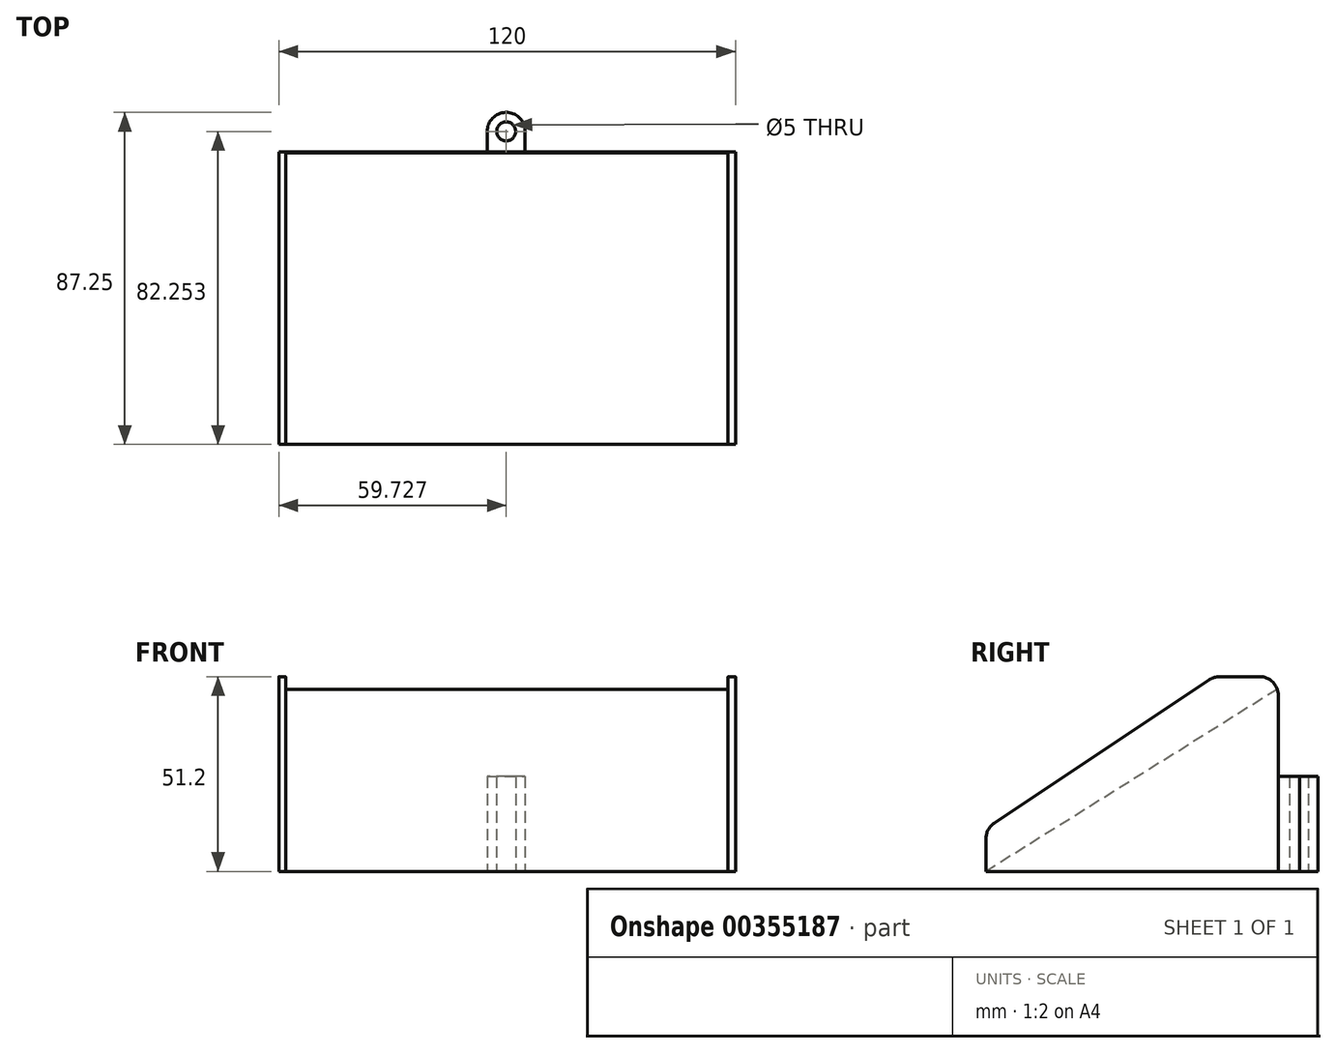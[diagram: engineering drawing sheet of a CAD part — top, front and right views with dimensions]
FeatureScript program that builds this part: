
annotation { "Feature Type Name" : "Feature", "Feature Type Description" : "" }
export const myFeature = defineFeature(function(context is Context, id is Id, definition is map)
    precondition{}
    {
        {
            var Q0;
            Q0=qCreatedBy(makeId("Top.planeOp"),FACE);
            var sketch = newSketch(context, id + "F0", { "sketchPlane" : qUnion([Q0])});
            skLineSegment(sketch, "E0.bottom", {"start": v(-59.62, 37.09) * mm, "end": v(60.38, 37.09) * mm});
            skLineSegment(sketch, "E0.top", {"start": v(-59.62, -39.78) * mm, "end": v(60.38, -39.78) * mm});
            skLineSegment(sketch, "E0.left", {"start": v(-59.62, 37.09) * mm, "end": v(-59.62, -39.78) * mm});
            skLineSegment(sketch, "E0.right", {"start": v(60.38, 37.09) * mm, "end": v(60.38, -39.78) * mm});
            skLineSegment(sketch, "E1", {"start": v(-57.82, 37.09) * mm, "end": v(-57.82, -39.78) * mm});
            skLineSegment(sketch, "E2", {"start": v(58.4, 37.09) * mm, "end": v(58.4, -39.78) * mm});
            skCircle(sketch, "E3", {"center": v(0.1, 42.47) * mm, "radius": 5 * mm});
            skCircle(sketch, "E4", {"center": v(0.1, 42.47) * mm, "radius": 2.5 * mm});
            skLineSegment(sketch, "E5", {"start": v(5.1, 42.69) * mm, "end": v(5.1, 37.09) * mm});
            skLineSegment(sketch, "E6", {"start": v(-4.9, 42.47) * mm, "end": v(-4.9, 37.09) * mm});
            skSolve(sketch);
        }
        {
            var Q0;
            Q0=makeQuery(id+"F0.imprint","IMPRINT",FACE,{"disambiguationData":[TD([[makeQuery(id+"F0.imprint","IMPRINT",EDGE,{"derivedFrom":sQuery(id+"F0.wireOp",EDGE,"E0.bottom")}),-1.0]])]});
            extrude(context, id + "F1", {"entities" : qUnion([Q0]), "depth" : 50 * mm});
        }
        {
            var Q0;
            Q0=makeQuery(id+"F1.opExtrude","CAP_EDGE",EDGE,{"disambiguationData":[OSD([sQuery(id+"F0.wireOp",EDGE,"E0.top")])],"isStart":false});
            chamfer(context, id + "F2", {"entities" : qUnion([Q0]), "chamferType" : ChamferType.TWO_OFFSETS, "width1" : 80 * mm, "oppositeDirection" : false, "width2" : 50 * mm, "tangentPropagation" : true});
        }
        {
            var Q0;
            Q0=makeQuery(id+"F0.imprint","IMPRINT",FACE,{"disambiguationData":[TD([[makeQuery(id+"F0.imprint","IMPRINT",EDGE,{"derivedFrom":sQuery(id+"F0.wireOp",EDGE,"E3")}),1.0]])]});
            var Q1;
            {var subQ3=sQuery(id+"F0.wireOp",EDGE,"E6");Q1=makeQuery(id+"F0.imprint","IMPRINT",FACE,{"disambiguationData":[TD([[makeQuery(id+"F0.imprint","IMPRINT",EDGE,{"derivedFrom":subQ3}),1.0]])]});}
            var Q2;
            {var subQ0=sQuery(id+"F0.wireOp",EDGE,"E5");var subQ1=sQuery(id+"F0.wireOp",EDGE,"E0.bottom");var subQ2=makeQuery(id+"F0.imprint","INTERSECT",VERTEX,{"derivedFrom":[subQ1,subQ0]});Q2=makeQuery(id+"F0.imprint","IMPRINT",FACE,{"disambiguationData":[TD([[makeQuery(id+"F0.imprint","IMPRINT",EDGE,{"disambiguationData":[TD([[subQ2,1.0]])],"derivedFrom":subQ1}),1.0]])]});}
            extrude(context, id + "F3", {"entities" : qUnion([Q0, Q1, Q2]), "depth" : 25 * mm});
        }
        {
            var Q0;
            {var subQ0=sQuery(id+"F0.wireOp",EDGE,"E0.left");Q0=makeQuery(id+"F0.imprint","IMPRINT",FACE,{"disambiguationData":[TD([[makeQuery(id+"F0.imprint","IMPRINT",EDGE,{"derivedFrom":subQ0}),1.0]])]});}
            var Q1;
            {var subQ0=sQuery(id+"F0.wireOp",EDGE,"E0.right");Q1=makeQuery(id+"F0.imprint","IMPRINT",FACE,{"disambiguationData":[TD([[makeQuery(id+"F0.imprint","IMPRINT",EDGE,{"derivedFrom":subQ0}),-1.0]])]});}
            extrude(context, id + "F4", {"entities" : qUnion([Q0, Q1]), "operationType" : NewBodyOperationType.ADD, "depth" : 51.2 * mm});
        }
        {
            var Q0;
            {var subQ0=sQuery(id+"F0.wireOp",EDGE,"E0.top");Q0=makeQuery(id+"F4.opExtrude","CAP_EDGE",EDGE,{"disambiguationData":[OSD([subQ0]),TDD([makeQuery(id+"F0.imprint","IMPRINT",EDGE,{"disambiguationData":[TD([[makeQuery(id+"F0.imprint","INTERSECT",VERTEX,{"derivedFrom":[subQ0,sQuery(id+"F0.wireOp",EDGE,"E0.left")]}),-1.0]])],"derivedFrom":subQ0})])],"isStart":false});}
            var Q1;
            {var subQ0=sQuery(id+"F0.wireOp",EDGE,"E0.top");Q1=makeQuery(id+"F4.opExtrude","CAP_EDGE",EDGE,{"disambiguationData":[OSD([subQ0]),TDD([makeQuery(id+"F0.imprint","IMPRINT",EDGE,{"disambiguationData":[TD([[makeQuery(id+"F0.imprint","INTERSECT",VERTEX,{"derivedFrom":[subQ0,sQuery(id+"F0.wireOp",EDGE,"E0.right")]}),1.0]])],"derivedFrom":subQ0})])],"isStart":false});}
            chamfer(context, id + "F5", {"entities" : qUnion([Q0, Q1]), "chamferType" : ChamferType.TWO_OFFSETS, "width1" : 60 * mm, "oppositeDirection" : false, "width2" : 40 * mm, "tangentPropagation" : true});
        }
        {
            var Q0;
            {var subQ0=sQuery(id+"F0.wireOp",EDGE,"E0.bottom");Q0=makeQuery(id+"F4.opExtrude","CAP_EDGE",EDGE,{"disambiguationData":[OSD([subQ0]),TDD([makeQuery(id+"F0.imprint","IMPRINT",EDGE,{"disambiguationData":[TD([[makeQuery(id+"F0.imprint","INTERSECT",VERTEX,{"derivedFrom":[subQ0,sQuery(id+"F0.wireOp",EDGE,"E0.right")]}),1.0]])],"derivedFrom":subQ0})])],"isStart":false});}
            var Q1;
            {var subQ0=sQuery(id+"F0.wireOp",EDGE,"E2");var subQ1=sQuery(id+"F0.wireOp",EDGE,"E0.right");var subQ2=sQuery(id+"F0.wireOp",EDGE,"E0.top");Q1=makeQuery(id+"F5.opChamfer","BLEND_EDGE",EDGE,{"blendedFrom":[makeQuery(id+"F4.opExtrude","CAP_EDGE",EDGE,{"disambiguationData":[OSD([subQ2]),TDD([makeQuery(id+"F0.imprint","IMPRINT",EDGE,{"disambiguationData":[TD([[makeQuery(id+"F0.imprint","INTERSECT",VERTEX,{"derivedFrom":[subQ2,subQ1]}),1.0]])],"derivedFrom":subQ2})])],"isStart":false}),makeQuery(id+"F4.opExtrude","CAP_FACE",FACE,{"disambiguationData":[OSD([sQuery(id+"F0.wireOp",EDGE,"E0.bottom"),subQ2,subQ1,subQ0])],"isStart":false})],"blendedInto":[makeQuery(id+"F4.opExtrude","CAP_FACE",FACE,{"disambiguationData":[OSD([sQuery(id+"F0.wireOp",EDGE,"E0.bottom"),subQ2,subQ1,subQ0])],"isStart":false})]});}
            var Q2;
            {var subQ0=sQuery(id+"F0.wireOp",EDGE,"E1");var subQ1=sQuery(id+"F0.wireOp",EDGE,"E0.left");var subQ2=sQuery(id+"F0.wireOp",EDGE,"E0.top");Q2=makeQuery(id+"F5.opChamfer","BLEND_EDGE",EDGE,{"blendedFrom":[makeQuery(id+"F4.opExtrude","CAP_EDGE",EDGE,{"disambiguationData":[OSD([subQ2]),TDD([makeQuery(id+"F0.imprint","IMPRINT",EDGE,{"disambiguationData":[TD([[makeQuery(id+"F0.imprint","INTERSECT",VERTEX,{"derivedFrom":[subQ2,subQ1]}),-1.0]])],"derivedFrom":subQ2})])],"isStart":false}),makeQuery(id+"F4.opExtrude","CAP_FACE",FACE,{"disambiguationData":[OSD([sQuery(id+"F0.wireOp",EDGE,"E0.bottom"),subQ2,subQ1,subQ0])],"isStart":false})],"blendedInto":[makeQuery(id+"F4.opExtrude","CAP_FACE",FACE,{"disambiguationData":[OSD([sQuery(id+"F0.wireOp",EDGE,"E0.bottom"),subQ2,subQ1,subQ0])],"isStart":false})]});}
            var Q3;
            {var subQ0=sQuery(id+"F0.wireOp",EDGE,"E0.top");var subQ1=makeQuery(id+"F0.imprint","IMPRINT",EDGE,{"disambiguationData":[TD([[makeQuery(id+"F0.imprint","INTERSECT",VERTEX,{"derivedFrom":[subQ0,sQuery(id+"F0.wireOp",EDGE,"E0.right")]}),1.0]])],"derivedFrom":subQ0});Q3=makeQuery(id+"F5.opChamfer","BLEND_EDGE",EDGE,{"blendedFrom":[makeQuery(id+"F4.opExtrude","CAP_EDGE",EDGE,{"disambiguationData":[OSD([subQ0]),TDD([subQ1])],"isStart":false}),makeQuery(id+"F4.opExtrude","SWEPT_FACE",FACE,{"disambiguationData":[OSD([subQ0]),TDD([subQ1])]})],"blendedInto":[makeQuery(id+"F4.opExtrude","SWEPT_FACE",FACE,{"disambiguationData":[OSD([subQ0]),TDD([subQ1])]})]});}
            var Q4;
            {var subQ0=sQuery(id+"F0.wireOp",EDGE,"E0.top");var subQ1=makeQuery(id+"F0.imprint","IMPRINT",EDGE,{"disambiguationData":[TD([[makeQuery(id+"F0.imprint","INTERSECT",VERTEX,{"derivedFrom":[subQ0,sQuery(id+"F0.wireOp",EDGE,"E0.left")]}),-1.0]])],"derivedFrom":subQ0});Q4=makeQuery(id+"F5.opChamfer","BLEND_EDGE",EDGE,{"blendedFrom":[makeQuery(id+"F4.opExtrude","CAP_EDGE",EDGE,{"disambiguationData":[OSD([subQ0]),TDD([subQ1])],"isStart":false}),makeQuery(id+"F4.opExtrude","SWEPT_FACE",FACE,{"disambiguationData":[OSD([subQ0]),TDD([subQ1])]})],"blendedInto":[makeQuery(id+"F4.opExtrude","SWEPT_FACE",FACE,{"disambiguationData":[OSD([subQ0]),TDD([subQ1])]})]});}
            fillet(context, id + "F6", {"entities" : qUnion([Q0, Q1, Q2, Q3, Q4]), "radius" : 5 * mm, "tangentPropagation" : true, "allowEdgeOverflow" : false});
        }
    });
